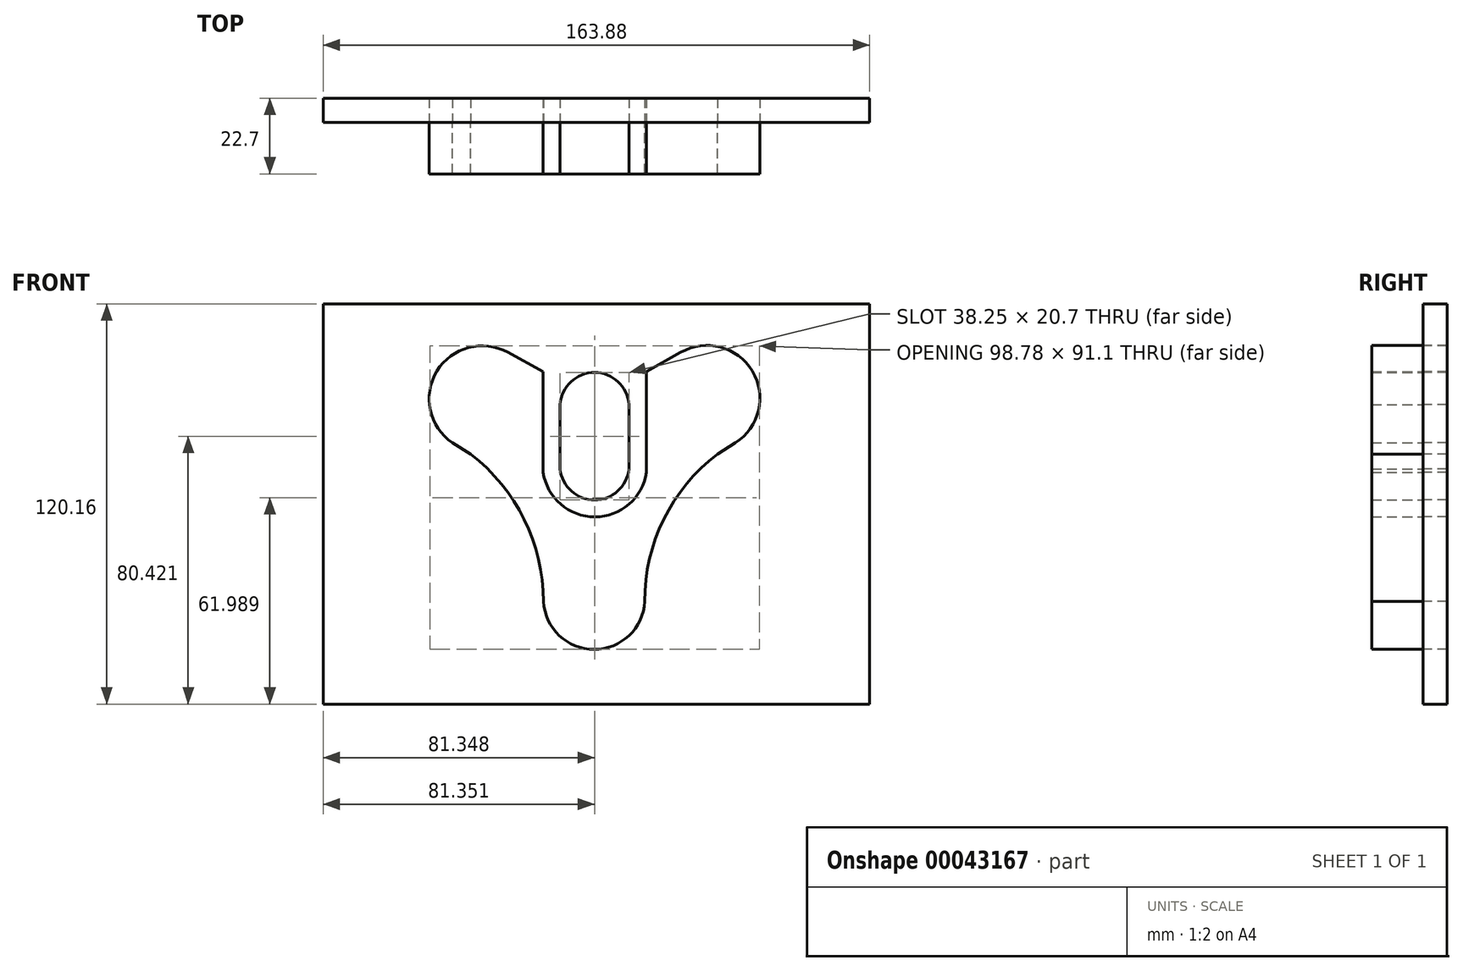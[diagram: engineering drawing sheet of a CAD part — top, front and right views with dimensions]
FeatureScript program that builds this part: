
annotation { "Feature Type Name" : "Feature", "Feature Type Description" : "" }
export const myFeature = defineFeature(function(context is Context, id is Id, definition is map)
    precondition{}
    {
        {
            var Q0;
            Q0=qCreatedBy(makeId("Front.planeOp"),FACE);
            var sketch = newSketch(context, id + "F0", { "sketchPlane" : qUnion([Q0])});
            skLineSegment(sketch, "E0", {"start": v(-10.94, 29.86) * mm, "end": v(-10.94, 10.45) * mm});
            skLineSegment(sketch, "E1", {"start": v(9.76, 29.86) * mm, "end": v(9.76, 10.45) * mm});
            skArc(sketch, "E2", {"start": v(-10.94, 10.45) * mm, "mid": v(-0.59, 1.22) * mm, "end": v(9.76, 10.45) * mm});
            skArc(sketch, "E3", {"start": v(9.76, 29.86) * mm, "mid": v(-0.59, 39.46) * mm, "end": v(-10.94, 29.86) * mm});
            skLineSegment(sketch, "E4", {"start": v(14.96, 39.72) * mm, "end": v(14.96, 9.5) * mm});
            skLineSegment(sketch, "E5", {"start": v(-16, 9.5) * mm, "end": v(-16, 39.72) * mm});
            skArc(sketch, "E6", {"start": v(-16, 9.5) * mm, "mid": v(-0.52, -3.9) * mm, "end": v(14.96, 9.5) * mm});
            skArc(sketch, "E7", {"start": v(-15.9, -29.26) * mm, "mid": v(-21.7, -4.65) * mm, "end": v(-37.7, 14.93) * mm});
            skArc(sketch, "E8", {"start": v(-15.9, -29.26) * mm, "mid": v(-0.72, -43.64) * mm, "end": v(14.46, -29.26) * mm});
            skArc(sketch, "E9", {"start": v(36.27, 14.93) * mm, "mid": v(20.15, -4.6) * mm, "end": v(14.46, -29.26) * mm});
            skLineSegment(sketch, "E10", {"start": v(14.96, 39.72) * mm, "end": v(25.29, 45.52) * mm});
            skLineSegment(sketch, "E11", {"start": v(36.27, 14.93) * mm, "end": v(41.65, 18.35) * mm});
            skLineSegment(sketch, "E12", {"start": v(-43.26, 18.35) * mm, "end": v(-37.7, 14.93) * mm});
            skLineSegment(sketch, "E13", {"start": v(-16, 39.72) * mm, "end": v(-26.58, 45.52) * mm});
            skArc(sketch, "E14", {"start": v(41.65, 18.35) * mm, "mid": v(46.72, 39.91) * mm, "end": v(25.29, 45.52) * mm});
            skArc(sketch, "E15", {"start": v(-26.58, 45.52) * mm, "mid": v(-47.86, 39.87) * mm, "end": v(-43.26, 18.35) * mm});
            skLineSegment(sketch, "E16.rect.bottom", {"start": v(-81.94, 60.08) * mm, "end": v(81.94, 60.08) * mm});
            skLineSegment(sketch, "E16.rect.top", {"start": v(-81.94, -60.08) * mm, "end": v(81.94, -60.08) * mm});
            skLineSegment(sketch, "E16.rect.left", {"start": v(-81.94, 60.08) * mm, "end": v(-81.94, -60.08) * mm});
            skLineSegment(sketch, "E16.rect.right", {"start": v(81.94, 60.08) * mm, "end": v(81.94, -60.08) * mm});
            skPoint(sketch, "E16.rect.middle", {"position": v(0, 0) * mm});
            skSolve(sketch);
        }
        {
            var Q0;
            Q0=makeQuery(id+"F0.imprint","IMPRINT",FACE,{"disambiguationData":[TD([[makeQuery(id+"F0.imprint","IMPRINT",EDGE,{"derivedFrom":sQuery(id+"F0.wireOp",EDGE,"E4")}),1.0]])]});
            var Q1;
            Q1=makeQuery(id+"F0.imprint","IMPRINT",FACE,{"disambiguationData":[TD([[makeQuery(id+"F0.imprint","IMPRINT",EDGE,{"derivedFrom":sQuery(id+"F0.wireOp",EDGE,"E0")}),1.0]])]});
            extrude(context, id + "F1", {"entities" : qUnion([Q0, Q1]), "depth" : 15.4 * mm});
        }
        {
            var Q0;
            Q0=makeQuery(id+"F0.imprint","IMPRINT",FACE,{"disambiguationData":[TD([[makeQuery(id+"F0.imprint","IMPRINT",EDGE,{"derivedFrom":sQuery(id+"F0.wireOp",EDGE,"E0")}),-1.0]])]});
            extrude(context, id + "F2", {"entities" : qUnion([Q0]), "oppositeDirection" : true, "depth" : 7.3 * mm});
        }
    });
